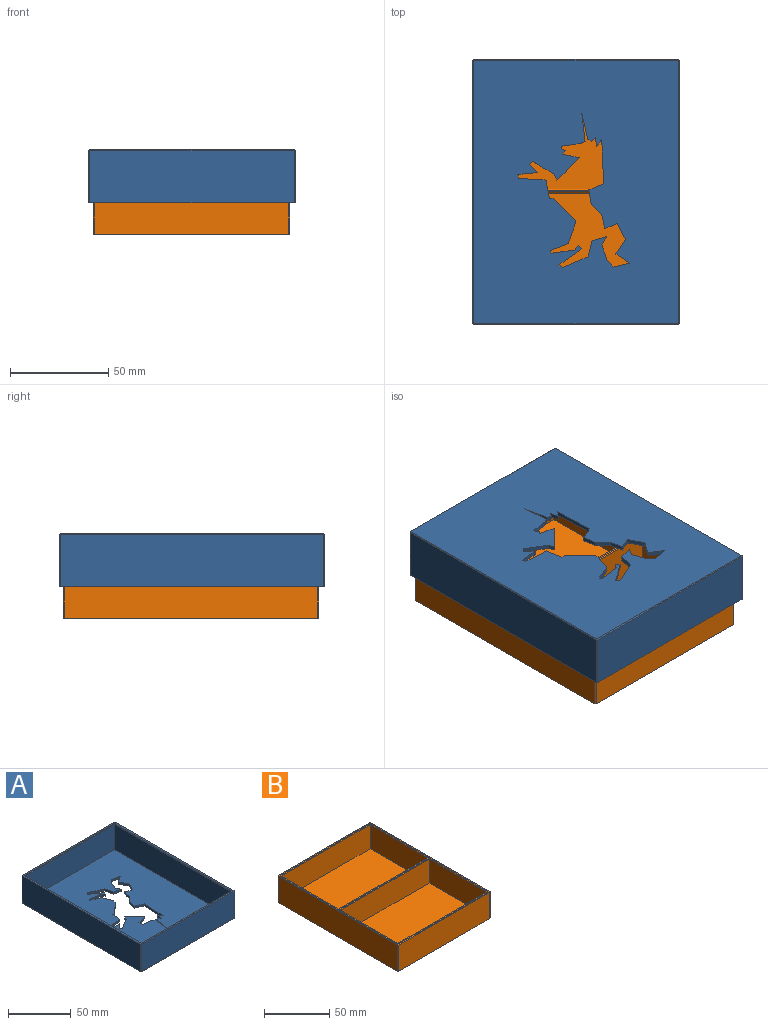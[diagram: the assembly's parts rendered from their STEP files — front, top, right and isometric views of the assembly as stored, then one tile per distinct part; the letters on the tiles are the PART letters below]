
ASSEMBLY  parts=2 mates=1
PART A: 76 faces, bbox 105x135x27 mm
  f0: plane 134x104mm, normal (0,0,-1), area 12622.5mm2, adj f18,f19,f23,f24,f27,f28,f29,f30
  f1: plane 131x101mm, normal (0,0,1), area 11917.5mm2, adj f6,f7,f8,f9,f27,f28,f29,f30
  f2: plane 134x26.5mm, normal (-1,0,0), area 3551mm2, adj f10,f20,f24,f26
  f3: plane 104x26.5mm, normal (0,-1,0), area 2756mm2, adj f10,f17,f23,f26
  f4: plane 134x26.5mm, normal (1,0,0), area 3551mm2, adj f10,f15,f17,f18
  f5: plane 104x26.5mm, normal (0,1,0), area 2756mm2, adj f10,f15,f19,f20
  f6: plane 101x24.5mm, normal (0,1,0), area 2474.5mm2, adj f1,f7,f9,f12
  f7: plane 131x24.5mm, normal (1,0,0), area 3209.5mm2, adj f1,f6,f8,f11
  f8: plane 101x24.5mm, normal (0,-1,0), area 2474.5mm2, adj f1,f7,f9,f13
  f9: plane 131x24.5mm, normal (-1,0,0), area 3209.5mm2, adj f1,f6,f8,f14
  f10: plane 135x105mm, normal (0,0,1), area 710.5mm2, adj f2,f3,f4,f5,f11,f12,f13,f14
  f11: plane 132x0.5mm, normal (0.71,0,0.71), area 93mm2, adj f7,f10,f12,f13
  f12: plane 102x0.5mm, normal (0,0.71,0.71), area 71.8mm2, adj f6,f10,f11,f14
  f13: plane 102x0.5mm, normal (0,-0.71,0.71), area 71.8mm2, adj f8,f10,f11,f14
  f14: plane 132x0.5mm, normal (-0.71,0,0.71), area 93mm2, adj f9,f10,f12,f13
  f15: plane 26.5x0.5mm, normal (0.71,0.71,0), area 18.7mm2, adj f4,f5,f10,f16
  f16: plane 0.5x0.5mm, normal (0.58,0.58,-0.58), area 0.2mm2, adj f15,f18,f19
  f17: plane 26.5x0.5mm, normal (0.71,-0.71,0), area 18.7mm2, adj f3,f4,f10,f21
  f18: plane 134x0.5mm, normal (0.71,0,-0.71), area 94.8mm2, adj f0,f4,f16,f21
  f19: plane 104x0.5mm, normal (0,0.71,-0.71), area 73.5mm2, adj f0,f5,f16,f22
  f20: plane 26.5x0.5mm, normal (-0.71,0.71,0), area 18.7mm2, adj f2,f5,f10,f22
  f21: plane 0.5x0.5mm, normal (0.58,-0.58,-0.58), area 0.2mm2, adj f17,f18,f23
  f22: plane 0.5x0.5mm, normal (-0.58,0.58,-0.58), area 0.2mm2, adj f19,f20,f24
  f23: plane 104x0.5mm, normal (0,-0.71,-0.71), area 73.5mm2, adj f0,f3,f21,f25
  f24: plane 134x0.5mm, normal (-0.71,0,-0.71), area 94.8mm2, adj f0,f2,f22,f25
  f25: plane 0.5x0.5mm, normal (-0.58,-0.58,-0.58), area 0.2mm2, adj f23,f24,f26
  f26: plane 26.5x0.5mm, normal (-0.71,-0.71,0), area 18.7mm2, adj f2,f3,f10,f25
  f27: plane 13.6x3.06mm, normal (-0.98,0.22,0), area 27.9mm2, adj f0,f1,f28,f75
  f28: plane 14.26x2mm, normal (0.99,-0.12,0), area 28.7mm2, adj f0,f1,f27,f29
  f29: plane 2.57x2mm, normal (0.44,0.9,0), area 5.7mm2, adj f0,f1,f28,f30
  f30: plane 9.2x2mm, normal (0.15,0.99,0), area 18.6mm2, adj f0,f1,f29,f31
  f31: plane 2x1.33mm, normal (0.97,0.23,0), area 2.7mm2, adj f0,f1,f30,f32
  f32: plane 2.1x2mm, normal (0.43,-0.9,0), area 4.7mm2, adj f0,f1,f31,f33
  f33: plane 2x1.64mm, normal (0.72,0.69,0), area 4.5mm2, adj f0,f1,f32,f34
  f34: plane 8.57x2mm, normal (0.22,-0.98,0), area 17.6mm2, adj f0,f1,f33,f35
  f35: plane 11.38x11.3mm, normal (0.7,0.71,0), area 32.1mm2, adj f0,f1,f34,f36
  f36: plane 2.88x2mm, normal (-0.91,0.42,0), area 6.3mm2, adj f0,f1,f35,f37
  f37: plane 11.15x6.78mm, normal (-0.52,0.85,0), area 26.1mm2, adj f0,f1,f36,f38
  f38: plane 2x1.79mm, normal (0.74,0.67,0), area 4.9mm2, adj f0,f1,f37,f39
  f39: plane 4.29x4.05mm, normal (0.69,-0.73,0), area 11.8mm2, adj f0,f1,f38,f40
  f40: plane 10.06x2mm, normal (0.09,1,0), area 20.2mm2, adj f0,f1,f39,f41
  f41: plane 2.03x2mm, normal (0.97,-0.22,0), area 4.2mm2, adj f0,f1,f40,f42
  f42: plane 13.88x2mm, normal (0.06,-1,0), area 27.8mm2, adj f0,f1,f41,f43
  f43: plane 9.43x2mm, normal (0.98,-0.18,0), area 19.2mm2, adj f0,f1,f42,f44
  f44: plane 2x1.87mm, normal (-0.12,-0.99,0), area 3.8mm2, adj f0,f1,f43,f45
  f45: plane 11.15x10.84mm, normal (0.7,-0.72,0), area 31.1mm2, adj f0,f1,f44,f46
  f46: plane 2.26x2mm, normal (1,-0.07,0), area 4.5mm2, adj f0,f1,f45,f47
  f47: plane 9.98x3.59mm, normal (0.94,0.34,0), area 21.2mm2, adj f0,f1,f46,f48
  f48: plane 9.2x3.59mm, normal (0.36,0.93,0), area 19.7mm2, adj f0,f1,f47,f49
  f49: plane 2x1.4mm, normal (0.85,-0.52,0), area 3.3mm2, adj f0,f1,f48,f50
  f50: plane 11.85x2mm, normal (-0.14,-0.99,0), area 23.9mm2, adj f0,f1,f49,f51
  f51: plane 2.49x2mm, normal (-0.82,-0.57,0), area 6.1mm2, adj f0,f1,f50,f52
  f52: plane 2x1.95mm, normal (0.78,-0.62,0), area 5mm2, adj f0,f1,f51,f53
  f53: plane 11.54x8.26mm, normal (0.58,0.81,0), area 28.4mm2, adj f0,f1,f52,f54
  f54: plane 2x1.79mm, normal (0.59,-0.8,0), area 4.5mm2, adj f0,f1,f53,f55
  f55: plane 13.1x5.61mm, normal (-0.39,-0.92,0), area 28.5mm2, adj f0,f1,f54,f56
  f56: plane 8.18x2.03mm, normal (-0.97,-0.24,0), area 16.9mm2, adj f0,f1,f55,f57
  f57: plane 7.52x2.03mm, normal (-0.26,-0.97,0), area 15.6mm2, adj f0,f1,f56,f58
  f58: plane 4.15x2.62mm, normal (0.85,0.53,0), area 9.8mm2, adj f0,f1,f57,f59
  f59: plane 7.48x2.62mm, normal (0.94,-0.33,0), area 15.8mm2, adj f0,f1,f58,f60
  f60: plane 3.96x3.44mm, normal (0.76,-0.66,0), area 10.5mm2, adj f0,f1,f59,f61
  f61: plane 8.29x2.07mm, normal (-0.24,-0.97,0), area 17.1mm2, adj f0,f1,f60,f62
  f62: plane 7.09x4.66mm, normal (-0.55,0.84,0), area 17mm2, adj f0,f1,f61,f63
  f63: plane 7.4x4.86mm, normal (-0.84,-0.55,0), area 17.7mm2, adj f0,f1,f62,f64
  f64: plane 8.14x4.23mm, normal (-0.89,0.46,0), area 18.4mm2, adj f0,f1,f63,f65
  f65: plane 6.31x2.69mm, normal (0.39,0.92,0), area 13.7mm2, adj f0,f1,f64,f66
  f66: plane 7.18x2mm, normal (-0.98,0.21,0), area 14.7mm2, adj f0,f1,f65,f67
  f67: plane 5.31x5.16mm, normal (-0.7,0.72,0), area 14.8mm2, adj f0,f1,f66,f68
  f68: plane 7.4x2mm, normal (-0.99,0.17,0), area 15mm2, adj f0,f1,f67,f69
  f69: plane 7.55x3.21mm, normal (-0.39,-0.92,0), area 16.4mm2, adj f0,f1,f68,f70
  f70: plane 22.35x2mm, normal (-1,0.04,0), area 44.7mm2, adj f0,f1,f69,f71
  f71: plane 3.29x2.62mm, normal (0.78,0.62,0), area 8.4mm2, adj f0,f1,f70,f72
  f72: plane 4.67x2mm, normal (-0.99,0.15,0), area 9.4mm2, adj f0,f1,f71,f73
  f73: plane 2.42x2mm, normal (0.77,0.64,0), area 6.3mm2, adj f0,f1,f72,f74
  f74: plane 2x1.27mm, normal (-0.64,0.77,0), area 3.3mm2, adj f0,f1,f73,f75
  f75: plane 2x0.52mm, normal (0,1,0), area 1mm2, adj f0,f1,f27,f74
PART B: 36 faces, bbox 100x130x25 mm
  f0: plane 129x24.5mm, normal (-1,0,0), area 3160.5mm2, adj f4,f21,f25,f27
  f1: plane 99x24.5mm, normal (0,-1,0), area 2425.5mm2, adj f4,f16,f20,f21
  f2: plane 129x24.5mm, normal (1,0,0), area 3160.5mm2, adj f4,f16,f18,f19
  f3: plane 99x24.5mm, normal (0,1,0), area 2425.5mm2, adj f4,f18,f24,f27
  f4: plane 130x100mm, normal (0,0,-1), area 12999.5mm2, adj f0,f1,f2,f3,f16,f18,f21,f27
  f5: plane 62x22.5mm, normal (1,0,0), area 1395mm2, adj f6,f12,f14,f31
  f6: plane 96x22.5mm, normal (0,-1,0), area 2160mm2, adj f5,f7,f14,f29
  f7: plane 62x22.5mm, normal (-1,0,0), area 1395mm2, adj f6,f12,f14,f28
  f8: plane 62x22.5mm, normal (1,0,0), area 1395mm2, adj f9,f11,f15,f33
  f9: plane 96x22.5mm, normal (0,-1,0), area 2160mm2, adj f8,f10,f15,f32
  f10: plane 62x22.5mm, normal (-1,0,0), area 1395mm2, adj f9,f11,f15,f34
  f11: plane 96x22.5mm, normal (0,1,0), area 2160mm2, adj f8,f10,f15,f35
  f12: plane 96x22.5mm, normal (0,1,0), area 2160mm2, adj f5,f7,f14,f30
  f13: plane 129x99mm, normal (0,0,1), area 549mm2, adj f19,f20,f24,f25,f28,f29,f30,f31
  f14: plane 96x62mm, normal (0,0,1), area 5952mm2, adj f5,f6,f7,f12
  f15: plane 96x62mm, normal (0,0,1), area 5952mm2, adj f8,f9,f10,f11
  f16: plane 24.5x0.5mm, normal (0.71,-0.71,0), area 17.3mm2, adj f1,f2,f4,f17
  f17: plane 0.5x0.5mm, normal (0.58,-0.58,0.58), area 0.2mm2, adj f16,f19,f20
  f18: plane 24.5x0.5mm, normal (0.71,0.71,0), area 17.3mm2, adj f2,f3,f4,f22
  f19: plane 129x0.5mm, normal (0.71,0,0.71), area 91.2mm2, adj f2,f13,f17,f22
  f20: plane 99x0.5mm, normal (0,-0.71,0.71), area 70mm2, adj f1,f13,f17,f23
  f21: plane 24.5x0.5mm, normal (-0.71,-0.71,0), area 17.3mm2, adj f0,f1,f4,f23
  f22: plane 0.5x0.5mm, normal (0.58,0.58,0.58), area 0.2mm2, adj f18,f19,f24
  f23: plane 0.5x0.5mm, normal (-0.58,-0.58,0.58), area 0.2mm2, adj f20,f21,f25
  f24: plane 99x0.5mm, normal (0,0.71,0.71), area 70mm2, adj f3,f13,f22,f26
  f25: plane 129x0.5mm, normal (-0.71,0,0.71), area 91.2mm2, adj f0,f13,f23,f26
  f26: plane 0.5x0.5mm, normal (-0.58,0.58,0.58), area 0.2mm2, adj f24,f25,f27
  f27: plane 24.5x0.5mm, normal (-0.71,0.71,0), area 17.3mm2, adj f0,f3,f4,f26
  f28: plane 63x0.5mm, normal (-0.71,0,0.71), area 44.2mm2, adj f7,f13,f29,f30
  f29: plane 97x0.5mm, normal (0,-0.71,0.71), area 68.2mm2, adj f6,f13,f28,f31
  f30: plane 97x0.5mm, normal (0,0.71,0.71), area 68.2mm2, adj f12,f13,f28,f31
  f31: plane 63x0.5mm, normal (0.71,0,0.71), area 44.2mm2, adj f5,f13,f29,f30
  f32: plane 97x0.5mm, normal (0,-0.71,0.71), area 68.2mm2, adj f9,f13,f33,f34
  f33: plane 63x0.5mm, normal (0.71,0,0.71), area 44.2mm2, adj f8,f13,f32,f35
  f34: plane 63x0.5mm, normal (-0.71,0,0.71), area 44.2mm2, adj f10,f13,f32,f35
  f35: plane 97x0.5mm, normal (0,0.71,0.71), area 68.2mm2, adj f11,f13,f33,f34
PLACE A rot(axis=(1,0,0),180deg) t=(-21.84,97.4,47.67)mm
PLACE B t=(-19.66,-34.57,8.87)mm fixed
MATE slider B.f4 <-> A.f0  axis (0,0,-1) through (30.34,30.43,6.87)mm
